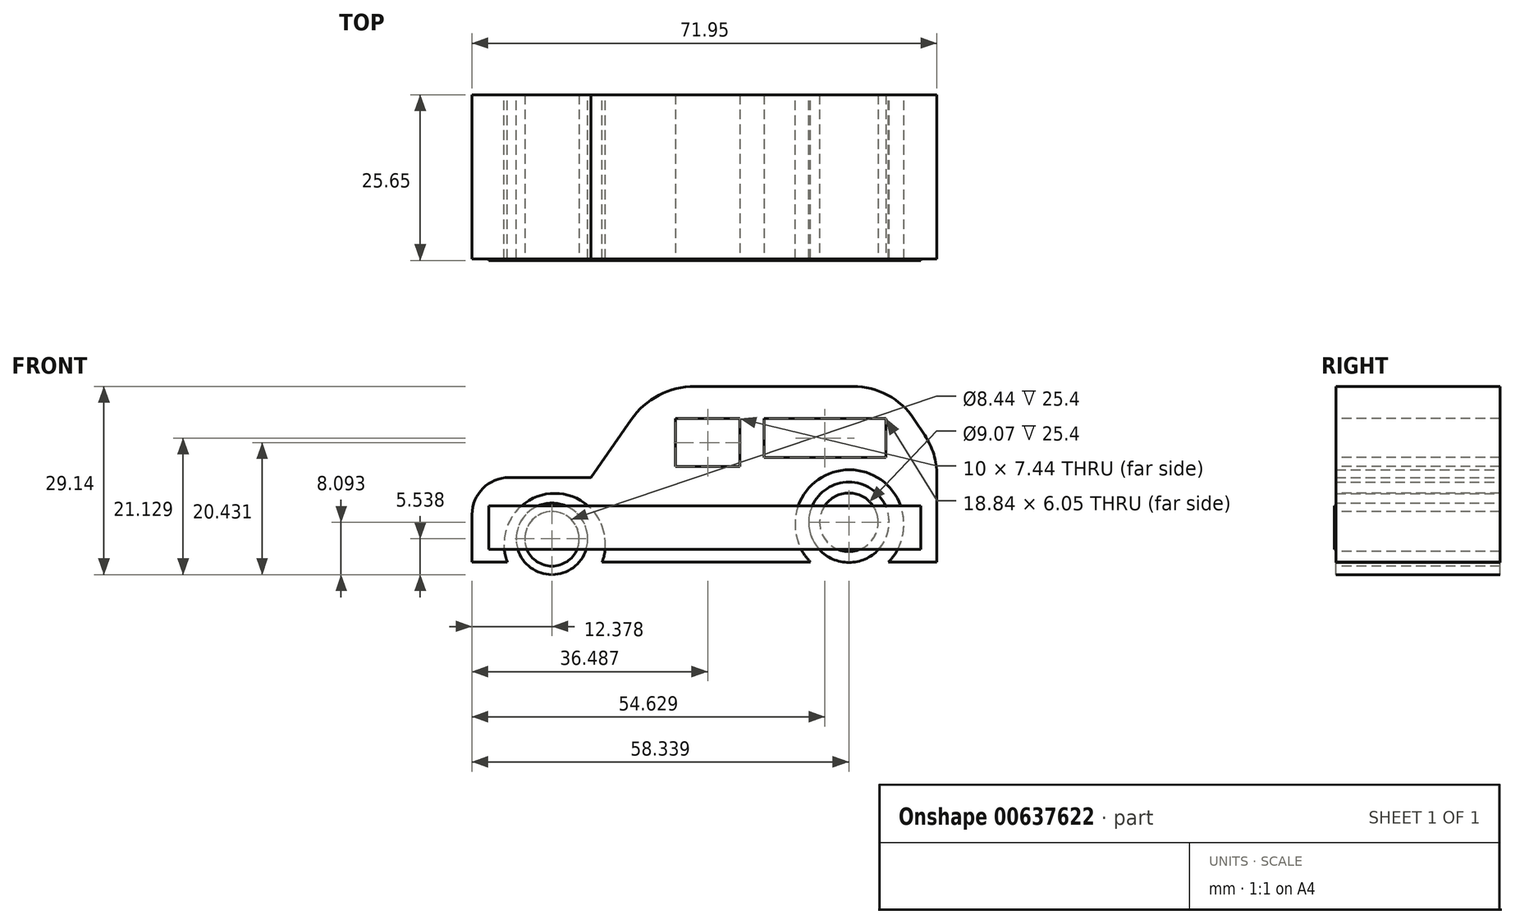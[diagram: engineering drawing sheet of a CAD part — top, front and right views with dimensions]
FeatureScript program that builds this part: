
annotation { "Feature Type Name" : "Feature", "Feature Type Description" : "" }
export const myFeature = defineFeature(function(context is Context, id is Id, definition is map)
    precondition{}
    {
        {
            var Q0;
            Q0=qCreatedBy(makeId("Front.planeOp"),FACE);
            var sketch = newSketch(context, id + "F0", { "sketchPlane" : qUnion([Q0])});
            skLineSegment(sketch, "E0", {"start": v(-57.42, 0) * mm, "end": v(-57.42, 7.34) * mm});
            skLineSegment(sketch, "E1", {"start": v(-51.66, 13.1) * mm, "end": v(-39, 13.1) * mm});
            skLineSegment(sketch, "E2", {"start": v(-39, 13.1) * mm, "end": v(-32.8, 22.04) * mm});
            skLineSegment(sketch, "E3", {"start": v(-22.93, 27.2) * mm, "end": v(0, 27.2) * mm});
            skLineSegment(sketch, "E4", {"start": v(0, 27.2) * mm, "end": v(1.56, 27.2) * mm});
            skLineSegment(sketch, "E5", {"start": v(11, 22.15) * mm, "end": v(12.66, 19.65) * mm});
            skLineSegment(sketch, "E6", {"start": v(14.53, 13.45) * mm, "end": v(14.53, 0) * mm});
            skLineSegment(sketch, "E7", {"start": v(14.53, 0) * mm, "end": v(7.05, 0) * mm});
            skArc(sketch, "E8", {"start": v(7.05, 0) * mm, "mid": v(1, 14.29) * mm, "end": v(-5.04, 0) * mm});
            skLineSegment(sketch, "E9", {"start": v(-5.04, 0) * mm, "end": v(-37.27, 0) * mm});
            skArc(sketch, "E10", {"start": v(-37.27, 0) * mm, "mid": v(-44.6, 10.63) * mm, "end": v(-51.95, 0) * mm});
            skLineSegment(sketch, "E11", {"start": v(-51.95, 0) * mm, "end": v(-57.42, 0) * mm});
            skPoint(sketch, "E12.visualSharp", {"position": v(-57.42, 13.1) * mm});
            skArc(sketch, "E12.filletArc", {"start": v(-51.66, 13.1) * mm, "mid": v(-55.73, 11.4) * mm, "end": v(-57.42, 7.34) * mm});
            skPoint(sketch, "E13.visualSharp", {"position": v(-29.21, 27.2) * mm});
            skArc(sketch, "E13.filletArc", {"start": v(-22.93, 27.2) * mm, "mid": v(-28.5, 25.83) * mm, "end": v(-32.8, 22.04) * mm});
            skPoint(sketch, "E14.visualSharp", {"position": v(7.63, 27.2) * mm});
            skArc(sketch, "E14.filletArc", {"start": v(11, 22.15) * mm, "mid": v(6.9, 25.86) * mm, "end": v(1.56, 27.2) * mm});
            skPoint(sketch, "E15.visualSharp", {"position": v(14.53, 16.84) * mm});
            skArc(sketch, "E15.filletArc", {"start": v(14.53, 13.45) * mm, "mid": v(14.05, 16.7) * mm, "end": v(12.66, 19.65) * mm});
            skSolve(sketch);
        }
        {
            var Q0;
            Q0 = qSketchRegion(id + "F0", true);
            extrude(context, id + "F1", {"entities" : qUnion([Q0]), "depth" : 25.4 * mm, "offsetDistance" : 25.4 * mm});
        }
        {
            var Q0;
            Q0=qCreatedBy(makeId("Front.planeOp"),FACE);
            var sketch = newSketch(context, id + "F2", { "sketchPlane" : qUnion([Q0])});
            skCircle(sketch, "E16", {"center": v(-45.04, 3.6) * mm, "radius": 5.54 * mm});
            skCircle(sketch, "E17", {"center": v(0.92, 6.15) * mm, "radius": 6.22 * mm});
            skSolve(sketch);
        }
        {
            var Q0;
            Q0=makeQuery(id+"F2.imprint","IMPRINT",FACE,{"disambiguationData":[TD([[makeQuery(id+"F2.imprint","IMPRINT",EDGE,{"derivedFrom":sQuery(id+"F2.wireOp",EDGE,"E16")}),1.0]])]});
            extrude(context, id + "F3", {"entities" : qUnion([Q0]), "depth" : 25.4 * mm, "offsetDistance" : 25.4 * mm});
        }
        {
            var Q0;
            Q0 = qSketchRegion(id + "F2", true);
            extrude(context, id + "F4", {"entities" : qUnion([Q0]), "operationType" : NewBodyOperationType.ADD, "depth" : 25.4 * mm, "offsetDistance" : 25.4 * mm});
        }
        {
            var Q0;
            Q0=makeQuery(id+"F1.opExtrude","CAP_FACE",FACE,{"disambiguationData":[OSD([sQuery(id+"F0.wireOp",EDGE,"E0"),sQuery(id+"F0.wireOp",EDGE,"E1"),sQuery(id+"F0.wireOp",EDGE,"E2"),sQuery(id+"F0.wireOp",EDGE,"E3"),sQuery(id+"F0.wireOp",EDGE,"E4"),sQuery(id+"F0.wireOp",EDGE,"E5"),sQuery(id+"F0.wireOp",EDGE,"E6"),sQuery(id+"F0.wireOp",EDGE,"E7"),sQuery(id+"F0.wireOp",EDGE,"E8"),sQuery(id+"F0.wireOp",EDGE,"E9"),sQuery(id+"F0.wireOp",EDGE,"E10"),sQuery(id+"F0.wireOp",EDGE,"E11"),sQuery(id+"F0.wireOp",EDGE,"E12.filletArc"),sQuery(id+"F0.wireOp",EDGE,"E13.filletArc"),sQuery(id+"F0.wireOp",EDGE,"E14.filletArc"),sQuery(id+"F0.wireOp",EDGE,"E15.filletArc")])],"isStart":false});
            var sketch = newSketch(context, id + "F5", { "sketchPlane" : qUnion([Q0])});
            skLineSegment(sketch, "E18", {"start": v(-25.93, 22.21) * mm, "end": v(-25.93, 14.77) * mm});
            skLineSegment(sketch, "E19", {"start": v(-25.93, 14.77) * mm, "end": v(-15.93, 14.77) * mm});
            skLineSegment(sketch, "E20", {"start": v(-15.93, 14.77) * mm, "end": v(-15.93, 22.21) * mm});
            skLineSegment(sketch, "E21", {"start": v(-15.93, 22.21) * mm, "end": v(-25.93, 22.21) * mm});
            skSolve(sketch);
        }
        {
            var Q0;
            Q0=makeQuery(id+"F5.imprint","IMPRINT",FACE,{"disambiguationData":[TD([[makeQuery(id+"F5.imprint","IMPRINT",EDGE,{"derivedFrom":sQuery(id+"F5.wireOp",EDGE,"E18")}),1.0]])]});
            extrude(context, id + "F6", {"entities" : qUnion([Q0]), "operationType" : NewBodyOperationType.REMOVE, "depth" : -25.4 * mm, "offsetDistance" : 25.4 * mm});
        }
        {
            var Q0;
            Q0=makeQuery(id+"F3.opExtrude","CAP_FACE",FACE,{"disambiguationData":[OSD([sQuery(id+"F2.wireOp",EDGE,"E16")])],"isStart":false});
            var sketch = newSketch(context, id + "F7", { "sketchPlane" : qUnion([Q0])});
            skCircle(sketch, "E22", {"center": v(-45.04, 3.6) * mm, "radius": 4.22 * mm});
            skSolve(sketch);
        }
        {
            var Q0;
            Q0=makeQuery(id+"F7.imprint","IMPRINT",FACE,{"disambiguationData":[TD([[makeQuery(id+"F7.imprint","IMPRINT",EDGE,{"derivedFrom":sQuery(id+"F7.wireOp",EDGE,"E22")}),1.0]])]});
            extrude(context, id + "F8", {"entities" : qUnion([Q0]), "operationType" : NewBodyOperationType.REMOVE, "oppositeDirection" : true, "depth" : 25.4 * mm, "offsetDistance" : 25.4 * mm});
        }
        {
            var Q0;
            Q0=makeQuery(id+"F4.opExtrude","CAP_FACE",FACE,{"disambiguationData":[OSD([sQuery(id+"F2.wireOp",EDGE,"E17")])],"isStart":false});
            var sketch = newSketch(context, id + "F9", { "sketchPlane" : qUnion([Q0])});
            skCircle(sketch, "E23", {"center": v(0.92, 6.15) * mm, "radius": 4.53 * mm});
            skSolve(sketch);
        }
        {
            var Q0;
            Q0=makeQuery(id+"F9.imprint","IMPRINT",FACE,{"disambiguationData":[TD([[makeQuery(id+"F9.imprint","IMPRINT",EDGE,{"derivedFrom":sQuery(id+"F9.wireOp",EDGE,"E23")}),1.0]])]});
            extrude(context, id + "F10", {"entities" : qUnion([Q0]), "operationType" : NewBodyOperationType.REMOVE, "oppositeDirection" : true, "depth" : 25.4 * mm, "offsetDistance" : 25.4 * mm});
        }
        {
            var Q0;
            Q0=makeQuery(id+"F1.opExtrude","CAP_FACE",FACE,{"disambiguationData":[OSD([sQuery(id+"F0.wireOp",EDGE,"E0"),sQuery(id+"F0.wireOp",EDGE,"E1"),sQuery(id+"F0.wireOp",EDGE,"E2"),sQuery(id+"F0.wireOp",EDGE,"E3"),sQuery(id+"F0.wireOp",EDGE,"E4"),sQuery(id+"F0.wireOp",EDGE,"E5"),sQuery(id+"F0.wireOp",EDGE,"E6"),sQuery(id+"F0.wireOp",EDGE,"E7"),sQuery(id+"F0.wireOp",EDGE,"E8"),sQuery(id+"F0.wireOp",EDGE,"E9"),sQuery(id+"F0.wireOp",EDGE,"E10"),sQuery(id+"F0.wireOp",EDGE,"E11"),sQuery(id+"F0.wireOp",EDGE,"E12.filletArc"),sQuery(id+"F0.wireOp",EDGE,"E13.filletArc"),sQuery(id+"F0.wireOp",EDGE,"E14.filletArc"),sQuery(id+"F0.wireOp",EDGE,"E15.filletArc")])],"isStart":false});
            var sketch = newSketch(context, id + "F11", { "sketchPlane" : qUnion([Q0])});
            skLineSegment(sketch, "E24.bottom", {"start": v(-12.21, 22.21) * mm, "end": v(6.63, 22.21) * mm});
            skLineSegment(sketch, "E24.top", {"start": v(-12.21, 16.17) * mm, "end": v(6.63, 16.17) * mm});
            skLineSegment(sketch, "E24.left", {"start": v(-12.21, 22.21) * mm, "end": v(-12.21, 16.17) * mm});
            skLineSegment(sketch, "E24.right", {"start": v(6.63, 22.21) * mm, "end": v(6.63, 16.17) * mm});
            skSolve(sketch);
        }
        {
            var Q0;
            Q0=makeQuery(id+"F11.imprint","IMPRINT",FACE,{"disambiguationData":[TD([[makeQuery(id+"F11.imprint","IMPRINT",EDGE,{"derivedFrom":sQuery(id+"F11.wireOp",EDGE,"E24.bottom")}),-1.0]])]});
            extrude(context, id + "F12", {"entities" : qUnion([Q0]), "operationType" : NewBodyOperationType.REMOVE, "oppositeDirection" : true, "depth" : 25.4 * mm, "offsetDistance" : 25.4 * mm});
        }
        {
            var Q0;
            Q0=makeQuery(id+"F1.opExtrude","CAP_FACE",FACE,{"disambiguationData":[OSD([sQuery(id+"F0.wireOp",EDGE,"E0"),sQuery(id+"F0.wireOp",EDGE,"E1"),sQuery(id+"F0.wireOp",EDGE,"E2"),sQuery(id+"F0.wireOp",EDGE,"E3"),sQuery(id+"F0.wireOp",EDGE,"E4"),sQuery(id+"F0.wireOp",EDGE,"E5"),sQuery(id+"F0.wireOp",EDGE,"E6"),sQuery(id+"F0.wireOp",EDGE,"E7"),sQuery(id+"F0.wireOp",EDGE,"E8"),sQuery(id+"F0.wireOp",EDGE,"E9"),sQuery(id+"F0.wireOp",EDGE,"E10"),sQuery(id+"F0.wireOp",EDGE,"E11"),sQuery(id+"F0.wireOp",EDGE,"E12.filletArc"),sQuery(id+"F0.wireOp",EDGE,"E13.filletArc"),sQuery(id+"F0.wireOp",EDGE,"E14.filletArc"),sQuery(id+"F0.wireOp",EDGE,"E15.filletArc")])],"isStart":false});
            var sketch = newSketch(context, id + "F13", { "sketchPlane" : qUnion([Q0])});
            skLineSegment(sketch, "E25.bottom", {"start": v(-54.83, 8.7) * mm, "end": v(12.03, 8.7) * mm});
            skLineSegment(sketch, "E25.top", {"start": v(-54.83, 1.94) * mm, "end": v(12.03, 1.94) * mm});
            skLineSegment(sketch, "E25.left", {"start": v(-54.83, 8.7) * mm, "end": v(-54.83, 1.94) * mm});
            skLineSegment(sketch, "E25.right", {"start": v(12.03, 8.7) * mm, "end": v(12.03, 1.94) * mm});
            skSolve(sketch);
        }
        {
            var Q0;
            {var subQ0=sQuery(id+"F13.wireOp",EDGE,"E25.bottom");var subQ1=makeQuery(id+"F1.opExtrude","CAP_EDGE",EDGE,{"disambiguationData":[OSD([sQuery(id+"F0.wireOp",EDGE,"E10")])],"isStart":false});var subQ2=makeQuery(id+"F13.imprint","INTERSECT",VERTEX,{"disambiguationData":[OD(1.0)],"derivedFrom":[subQ1,subQ0]});Q0=makeQuery(id+"F13.imprint","IMPRINT",FACE,{"disambiguationData":[TD([[makeQuery(id+"F13.imprint","IMPRINT",EDGE,{"disambiguationData":[TD([[subQ2,-1.0]])],"derivedFrom":subQ0}),-1.0]])]});}
            var Q1;
            {var subQ0=sQuery(id+"F13.wireOp",EDGE,"E25.left");Q1=makeQuery(id+"F13.imprint","IMPRINT",FACE,{"disambiguationData":[TD([[makeQuery(id+"F13.imprint","IMPRINT",EDGE,{"derivedFrom":subQ0}),1.0]])]});}
            var Q2;
            {var subQ0=sQuery(id+"F13.wireOp",EDGE,"E25.bottom");var subQ1=makeQuery(id+"F1.opExtrude","CAP_EDGE",EDGE,{"disambiguationData":[OSD([sQuery(id+"F0.wireOp",EDGE,"E10")])],"isStart":false});var subQ2=makeQuery(id+"F13.imprint","INTERSECT",VERTEX,{"disambiguationData":[OD(0.0)],"derivedFrom":[subQ1,subQ0]});Q2=makeQuery(id+"F13.imprint","IMPRINT",FACE,{"disambiguationData":[TD([[makeQuery(id+"F13.imprint","IMPRINT",EDGE,{"disambiguationData":[TD([[subQ2,-1.0]])],"derivedFrom":subQ0}),-1.0]])]});}
            var Q3;
            {var subQ0=sQuery(id+"F13.wireOp",EDGE,"E25.bottom");var subQ1=makeQuery(id+"F1.opExtrude","CAP_EDGE",EDGE,{"disambiguationData":[OSD([sQuery(id+"F0.wireOp",EDGE,"E8")])],"isStart":false});var subQ2=makeQuery(id+"F13.imprint","INTERSECT",VERTEX,{"disambiguationData":[OD(0.0)],"derivedFrom":[subQ1,subQ0]});Q3=makeQuery(id+"F13.imprint","IMPRINT",FACE,{"disambiguationData":[TD([[makeQuery(id+"F13.imprint","IMPRINT",EDGE,{"disambiguationData":[TD([[subQ2,-1.0]])],"derivedFrom":subQ0}),-1.0]])]});}
            var Q4;
            {var subQ0=sQuery(id+"F13.wireOp",EDGE,"E25.right");Q4=makeQuery(id+"F13.imprint","IMPRINT",FACE,{"disambiguationData":[TD([[makeQuery(id+"F13.imprint","IMPRINT",EDGE,{"derivedFrom":subQ0}),-1.0]])]});}
            extrude(context, id + "F14", {"entities" : qUnion([Q0, Q1, Q2, Q3, Q4]), "depth" : 0.25 * mm, "offsetDistance" : 25.4 * mm});
        }
    });
